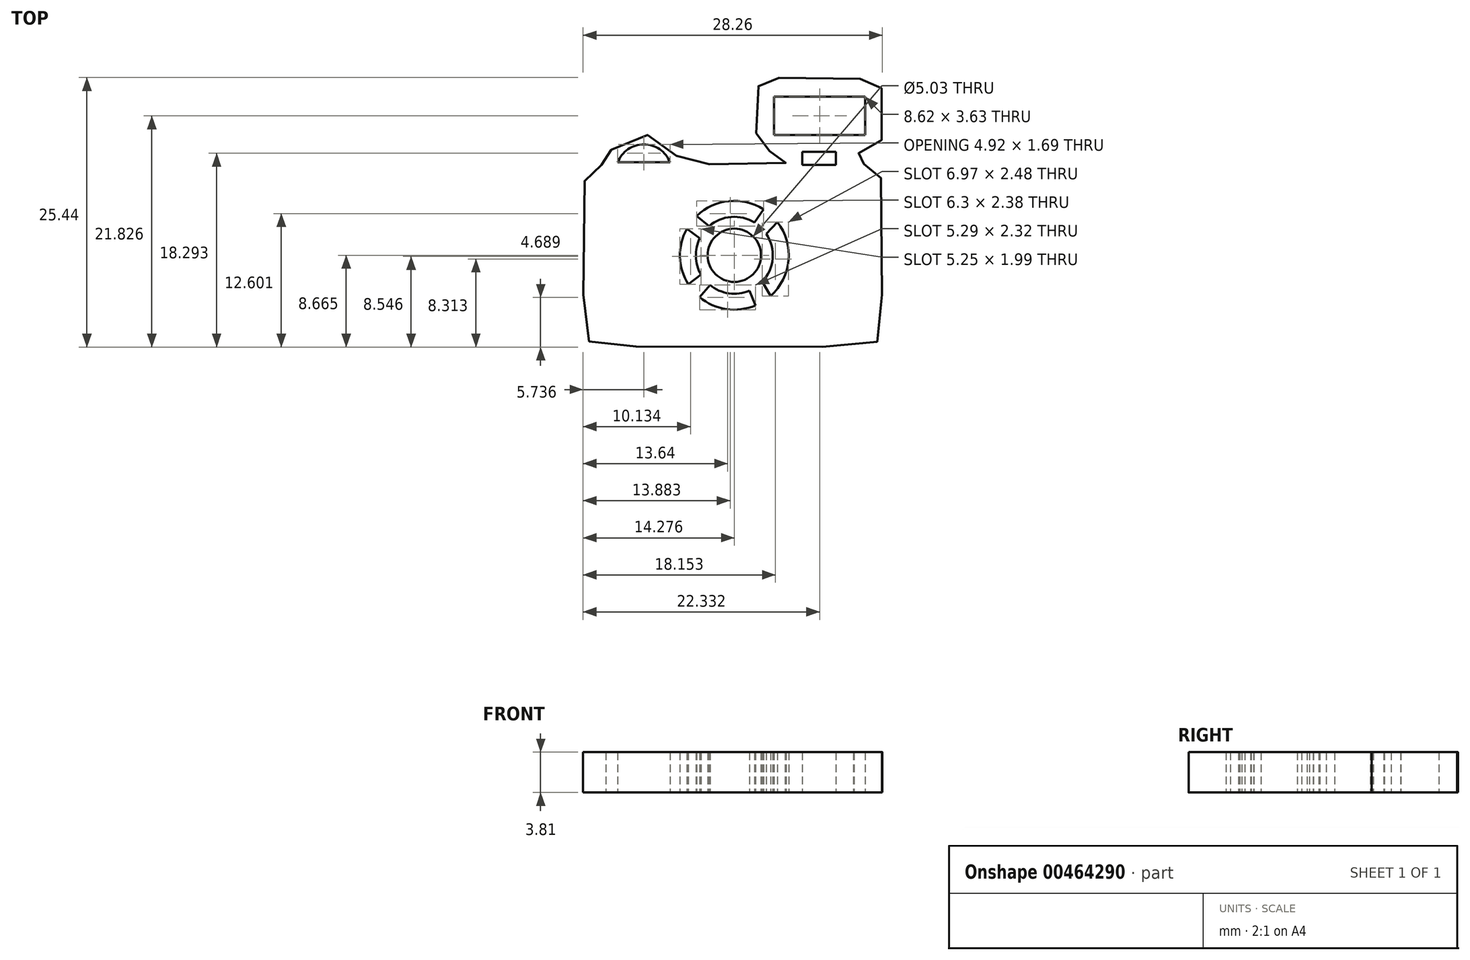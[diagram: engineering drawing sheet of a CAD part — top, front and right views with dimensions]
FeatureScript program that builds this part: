
annotation { "Feature Type Name" : "Feature", "Feature Type Description" : "" }
export const myFeature = defineFeature(function(context is Context, id is Id, definition is map)
    precondition{}
    {
        {
            var Q0;
            Q0=qCreatedBy(makeId("Top.planeOp"),FACE);
            var sketch = newSketch(context, id + "F0", { "sketchPlane" : qUnion([Q0])});
            skPoint(sketch, "E0.middle", {"position": v(0, 0) * mm});
            skArc(sketch, "E1", {"start": v(5.36, -10.02) * mm, "mid": v(7.06, -6.67) * mm, "end": v(6.02, -3.05) * mm});
            skLineSegment(sketch, "E2", {"start": v(5.7, 8.8) * mm, "end": v(5.7, 5.16) * mm});
            skLineSegment(sketch, "E3", {"start": v(5.7, 5.16) * mm, "end": v(14.31, 5.16) * mm});
            skLineSegment(sketch, "E4", {"start": v(14.31, 5.16) * mm, "end": v(14.31, 8.8) * mm});
            skLineSegment(sketch, "E5", {"start": v(14.31, 8.8) * mm, "end": v(5.7, 8.8) * mm});
            skFitSpline(sketch, "E6", {"points": [v(6.17, 10.57) * mm, v(13.6, 10.49) * mm, v(14.22, 10.49) * mm, v(14.83, 10.4) * mm, v(15.62, 9.87) * mm, v(15.88, 9.35) * mm, v(15.88, 4.97) * mm, v(15.88, 4.8) * mm, v(15.62, 4.19) * mm, v(15, 3.66) * mm, v(14.3, 3.49) * mm, v(13.26, 3.4) * mm, v(13.22, 3.24) * mm, v(13.22, 2.6) * mm, v(13.22, 2.48) * mm, v(14.42, 2.44) * mm, v(14.66, 2.36) * mm, v(15.46, 1.83) * mm, v(15.74, 1.27) * mm, v(15.82, 0.83) * mm, v(15.88, -13.28) * mm, v(15.88, -13.6) * mm, v(15.73, -14) * mm, v(15.26, -14.48) * mm, v(14.74, -14.79) * mm, v(14.06, -14.84) * mm, v(-10.38, -14.84) * mm, v(-10.72, -14.84) * mm, v(-11.26, -14.64) * mm, v(-12, -14.03) * mm, v(-12.2, -13.5) * mm, v(-12.27, -12.89) * mm, v(-12.22, 0.67) * mm, v(-12.16, 0.93) * mm, v(-12.11, 1.3) * mm, v(-11.54, 2.03) * mm, v(-10.6, 2.34) * mm, v(-10.3, 2.34) * mm, v(-10.19, 2.34) * mm, v(-10.19, 2.8) * mm, v(-10.08, 3.07) * mm, v(-9.56, 3.9) * mm, v(-8.26, 4.84) * mm, v(-6.44, 5.2) * mm, v(-4.88, 4.73) * mm, v(-3.9, 3.85) * mm, v(-3.32, 2.76) * mm, v(-3.27, 2.5) * mm, v(-3.22, 2.34) * mm, v(-2.9, 2.34) * mm, v(6.71, 2.36) * mm, v(6.83, 2.36) * mm, v(6.8, 2.6) * mm, v(6.75, 3.52) * mm, v(6.75, 3.64) * mm, v(6.6, 3.64) * mm, v(5.23, 3.64) * mm, v(5.1, 3.64) * mm, v(4.75, 3.88) * mm, v(4.22, 4.52) * mm, v(4.06, 4.8) * mm, v(3.94, 9.14) * mm, v(3.98, 9.38) * mm, v(4.22, 9.78) * mm, v(4.7, 10.22) * mm, v(5.36, 10.5) * mm, v(5.85, 10.53) * mm, v(6.17, 10.57) * mm]});
            skLineSegment(sketch, "E7", {"start": v(8.38, 3.59) * mm, "end": v(11.55, 3.59) * mm});
            skLineSegment(sketch, "E8", {"start": v(11.55, 3.59) * mm, "end": v(11.55, 2.35) * mm});
            skLineSegment(sketch, "E9", {"start": v(11.55, 2.35) * mm, "end": v(8.38, 2.35) * mm});
            skLineSegment(sketch, "E10", {"start": v(8.38, 2.35) * mm, "end": v(8.38, 3.59) * mm});
            skLineSegment(sketch, "E11", {"start": v(-9.06, 2.6) * mm, "end": v(-4.13, 2.6) * mm});
            skArc(sketch, "E12", {"start": v(-4.13, 2.6) * mm, "mid": v(-6.6, 4.29) * mm, "end": v(-9.06, 2.6) * mm});
            skArc(sketch, "E13", {"start": v(4.59, -8.68) * mm, "mid": v(5.57, -6.48) * mm, "end": v(4.96, -4.16) * mm});
            skCircle(sketch, "E14", {"center": v(1.95, -6.19) * mm, "radius": 2.52 * mm});
            skLineSegment(sketch, "E15", {"start": v(-2.54, -3.68) * mm, "end": v(-1.31, -4.58) * mm});
            skLineSegment(sketch, "E16", {"start": v(-1.6, -2.46) * mm, "end": v(-0.43, -3.44) * mm});
            skLineSegment(sketch, "E17", {"start": v(3.37, -9.53) * mm, "end": v(3.96, -10.91) * mm});
            skLineSegment(sketch, "E18", {"start": v(4.59, -8.68) * mm, "end": v(5.36, -10.02) * mm});
            skArc(sketch, "E19.trimOffspring", {"start": v(-2.54, -3.68) * mm, "mid": v(-3.19, -6.32) * mm, "end": v(-2.4, -8.93) * mm});
            skArc(sketch, "E20.trimOffspring", {"start": v(-1.31, -4.58) * mm, "mid": v(-1.69, -6.3) * mm, "end": v(-1.2, -8) * mm});
            skLineSegment(sketch, "E21", {"start": v(3.85, -3.1) * mm, "end": v(4.7, -1.85) * mm});
            skLineSegment(sketch, "E22", {"start": v(4.96, -4.16) * mm, "end": v(6.02, -3.05) * mm});
            skArc(sketch, "E23.trimOffspring", {"start": v(4.7, -1.85) * mm, "mid": v(1.45, -1.07) * mm, "end": v(-1.6, -2.46) * mm});
            skArc(sketch, "E24.trimOffspring", {"start": v(3.85, -3.1) * mm, "mid": v(1.66, -2.56) * mm, "end": v(-0.43, -3.44) * mm});
            skLineSegment(sketch, "E25", {"start": v(-1.2, -8) * mm, "end": v(-2.4, -8.93) * mm});
            skLineSegment(sketch, "E26", {"start": v(-0.35, -9) * mm, "end": v(-1.34, -10.14) * mm});
            skArc(sketch, "E27.trimOffspring", {"start": v(-0.35, -9) * mm, "mid": v(1.44, -9.78) * mm, "end": v(3.37, -9.53) * mm});
            skArc(sketch, "E28.trimOffspring", {"start": v(-1.34, -10.14) * mm, "mid": v(1.2, -11.27) * mm, "end": v(3.96, -10.91) * mm});
            skSolve(sketch);
        }
        {
            var Q0;
            Q0 = qSketchRegion(id + "F0", true);
            extrude(context, id + "F1", {"entities" : qUnion([Q0]), "depth" : 3.8 * mm});
        }
    });
